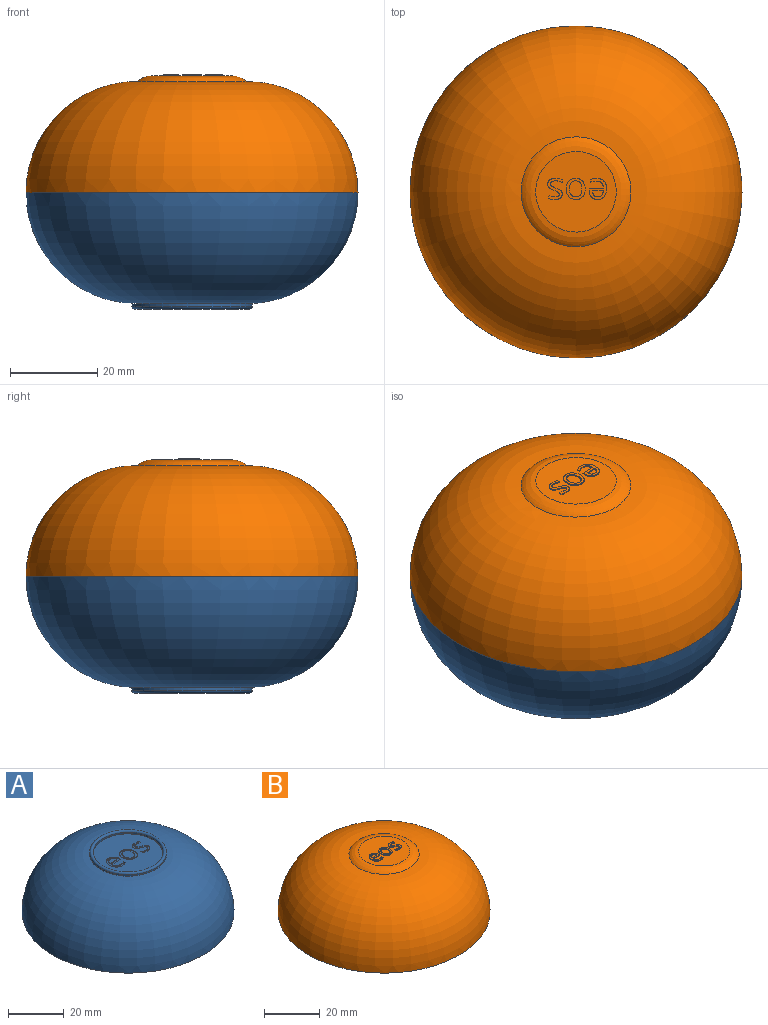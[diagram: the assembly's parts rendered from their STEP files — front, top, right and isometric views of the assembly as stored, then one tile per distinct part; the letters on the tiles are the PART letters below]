
ASSEMBLY  parts=2 mates=1
PART A: 74 faces, bbox 75.9x75.9x26.7 mm
  f0: plane 24.98x24.98mm, normal (0,0,1), area 425.6mm2, adj f4,f14,f15,f16,f17,f18,f19,f20
  f1: plane 75.95x75.95mm, normal (0,0,-1), area 339mm2, adj f2,f73
  f2: torus R=12.57mm, axis (0,0,1), area 7205.7mm2, adj f1,f5
  f3: cylinder r=13.76mm len=27.52mm, axis (0,0,-1), area 54.9mm2, adj f5,f6
  f4: cylinder r=12.49mm len=24.98mm, axis (0,0,-1), area 49.8mm2, adj f0,f6
  f5: plane 27.52x27.52mm, normal (0,0,-1), area 98mm2, adj f2,f3
  f6: torus R=13.12mm, axis (0,0,1), area 164.5mm2, adj f3,f4
  f7: extruded ~1.85x0.49mm, area 0.5mm2, adj f8,f23,f24,f71
  f8: extruded ~1.84x0.48mm, area 0.5mm2, adj f7,f9,f24,f71
  f9: extruded ~1.42x0.62mm, area 0.4mm2, adj f8,f10,f24,f71
  f10: extruded ~1.44x0.63mm, area 0.4mm2, adj f9,f11,f24,f71
  f11: extruded ~1.83x0.49mm, area 0.5mm2, adj f10,f12,f24,f71
  f12: extruded ~1.85x0.49mm, area 0.5mm2, adj f11,f13,f24,f71
  f13: extruded ~1.43x0.63mm, area 0.4mm2, adj f12,f23,f24,f71
  f14: extruded ~2.42x0.78mm, area 0.7mm2, adj f0,f15,f22,f24
  f15: extruded ~2.39x0.78mm, area 0.7mm2, adj f0,f14,f16,f24
  f16: extruded ~2.11x0.88mm, area 0.6mm2, adj f0,f15,f17,f24
  f17: extruded ~2.15x0.86mm, area 0.6mm2, adj f0,f16,f18,f24
  f18: extruded ~2.41x0.77mm, area 0.7mm2, adj f0,f17,f19,f24
  f19: extruded ~1.74x0.36mm, area 0.5mm2, adj f0,f18,f20,f24
  f20: extruded ~1.14x1.02mm, area 0.4mm2, adj f0,f19,f21,f24
  f21: extruded ~1.51x0.4mm, area 0.4mm2, adj f0,f20,f22,f24
  f22: extruded ~2.15x0.87mm, area 0.6mm2, adj f0,f14,f21,f24
  f23: extruded ~1.43x0.63mm, area 0.4mm2, adj f7,f13,f24,f71
  f24: plane 6.56x5.81mm, normal (0,0,1), area 15.4mm2, adj f7,f8,f9,f10,f11,f12,f13,f14
  f25: extruded ~1.21x0.5mm, area 0.3mm2, adj f26,f43,f44,f72
  f26: extruded ~1.16x0.48mm, area 0.3mm2, adj f25,f27,f44,f72
  f27: extruded ~1.39x0.4mm, area 0.4mm2, adj f26,f28,f44,f72
  f28: plane 3.31x0.25mm, normal (0,-1,0), area 0.8mm2, adj f27,f43,f44,f72
  f29: extruded ~2.21x0.86mm, area 0.6mm2, adj f0,f30,f42,f44
  f30: extruded ~1.09x0.25mm, area 0.3mm2, adj f0,f29,f31,f44
  f31: extruded ~0.96x0.31mm, area 0.3mm2, adj f0,f30,f32,f44
  f32: plane 0.86x0.25mm, normal (-1,0,0), area 0.2mm2, adj f0,f31,f33,f44
  f33: extruded ~2.02x0.43mm, area 0.5mm2, adj f0,f32,f34,f44
  f34: extruded ~1.5x0.58mm, area 0.4mm2, adj f0,f33,f35,f44
  f35: extruded ~1.69x0.56mm, area 0.5mm2, adj f0,f34,f36,f44
  f36: plane 4.36x0.25mm, normal (0,1,0), area 1.1mm2, adj f0,f35,f37,f44
  f37: plane 0.61x0.25mm, normal (-1,0,0), area 0.2mm2, adj f0,f36,f38,f44
  f38: extruded ~2.06x0.69mm, area 0.6mm2, adj f0,f37,f39,f44
  f39: extruded ~1.88x0.78mm, area 0.5mm2, adj f0,f38,f40,f44
  f40: extruded ~2.03x0.9mm, area 0.6mm2, adj f0,f39,f41,f44
  f41: extruded ~2.43x0.75mm, area 0.7mm2, adj f0,f40,f42,f44
  f42: extruded ~2.37x0.81mm, area 0.7mm2, adj f0,f29,f41,f44
  f43: extruded ~1.37x0.54mm, area 0.4mm2, adj f25,f28,f44,f72
  f44: plane 6.56x5.35mm, normal (0,0,1), area 16mm2, adj f25,f26,f27,f28,f29,f30,f31,f32
  f45: extruded ~1.36x0.66mm, area 0.4mm2, adj f0,f46,f69,f70
  f46: extruded ~1.05x0.4mm, area 0.3mm2, adj f0,f45,f47,f70
  f47: extruded ~1.52x0.83mm, area 0.4mm2, adj f0,f46,f48,f70
  f48: extruded ~1.11x0.47mm, area 0.3mm2, adj f0,f47,f49,f70
  f49: extruded ~0.42x0.34mm, area 0.1mm2, adj f0,f48,f50,f70
  f50: extruded ~0.43x0.25mm, area 0.1mm2, adj f0,f49,f51,f70
  f51: extruded ~0.59x0.35mm, area 0.2mm2, adj f0,f50,f52,f70
  f52: extruded ~1.03x0.25mm, area 0.3mm2, adj f0,f51,f53,f70
  f53: extruded ~1.73x0.39mm, area 0.5mm2, adj f0,f52,f54,f70
  f54: plane 0.78x0.34mm, normal (-0.92,0.4,0), area 0.2mm2, adj f0,f53,f55,f70
  f55: extruded ~2x0.42mm, area 0.5mm2, adj f0,f54,f56,f70
  f56: extruded ~1.73x0.45mm, area 0.5mm2, adj f0,f55,f57,f70
  f57: extruded ~1.22x0.63mm, area 0.4mm2, adj f0,f56,f58,f70
  f58: extruded ~0.74x0.25mm, area 0.2mm2, adj f0,f57,f59,f70
  f59: extruded ~0.56x0.55mm, area 0.2mm2, adj f0,f58,f60,f70
  f60: extruded ~1.26x0.57mm, area 0.4mm2, adj f0,f59,f61,f70
  f61: extruded ~1.25x0.62mm, area 0.4mm2, adj f0,f60,f62,f70
  f62: extruded ~0.63x0.32mm, area 0.2mm2, adj f0,f61,f63,f70
  f63: extruded ~0.73x0.4mm, area 0.2mm2, adj f0,f62,f64,f70
  f64: extruded ~1.15x0.25mm, area 0.3mm2, adj f0,f63,f65,f70
  f65: extruded ~1.01x0.25mm, area 0.3mm2, adj f0,f64,f66,f70
  f66: extruded ~0.98x0.36mm, area 0.3mm2, adj f0,f65,f67,f70
  f67: plane 0.89x0.25mm, normal (1,0,0), area 0.2mm2, adj f0,f66,f68,f70
  f68: extruded ~1.96x0.4mm, area 0.5mm2, adj f0,f67,f69,f70
  f69: extruded ~1.85x0.48mm, area 0.5mm2, adj f0,f45,f68,f70
  f70: plane 6.56x4.49mm, normal (0,0,1), area 12.3mm2, adj f45,f46,f47,f48,f49,f50,f51,f52
  f71: plane 4.94x3.83mm, normal (0,0,1), area 15.7mm2, adj f7,f8,f9,f10,f11,f12,f13,f23
  f72: plane 3.31x1.87mm, normal (0,0,1), area 5mm2, adj f25,f26,f27,f28,f43
  f73: sphere r=40.23mm, area 5905.9mm2, adj f1
PART B: 71 faces, bbox 75.9x75.9x26.9 mm
  f0: plane 18.43x18.43mm, normal (0,0,1), area 231.5mm2, adj f3,f8,f9,f10,f11,f12,f13,f14
  f1: plane 75.95x75.95mm, normal (0,0,-1), area 338.8mm2, adj f2,f70
  f2: torus R=12.57mm, axis (0,0,1), area 7205.6mm2, adj f1,f3
  f3: torus R=9.21mm, axis (0,0,-1), area 253.1mm2, adj f0,f2
  f4: extruded ~0.9x0.37mm, area 0.3mm2, adj f5,f22,f23,f24
  f5: extruded ~0.85x0.36mm, area 0.2mm2, adj f4,f6,f23,f24
  f6: extruded ~1.03x0.3mm, area 0.3mm2, adj f5,f7,f23,f24
  f7: plane 2.45x0.25mm, normal (0,1,0), area 0.6mm2, adj f6,f22,f23,f24
  f8: extruded ~1.64x0.63mm, area 0.5mm2, adj f0,f9,f21,f23
  f9: extruded ~0.81x0.25mm, area 0.2mm2, adj f0,f8,f10,f23
  f10: extruded ~0.71x0.25mm, area 0.2mm2, adj f0,f9,f11,f23
  f11: plane 0.63x0.25mm, normal (1,0,0), area 0.2mm2, adj f0,f10,f12,f23
  f12: extruded ~1.49x0.32mm, area 0.4mm2, adj f0,f11,f13,f23
  f13: extruded ~1.11x0.43mm, area 0.3mm2, adj f0,f12,f14,f23
  f14: extruded ~1.25x0.42mm, area 0.3mm2, adj f0,f13,f15,f23
  f15: plane 3.22x0.25mm, normal (0,-1,0), area 0.8mm2, adj f0,f14,f16,f23
  f16: plane 0.45x0.25mm, normal (1,0,0), area 0.1mm2, adj f0,f15,f17,f23
  f17: extruded ~1.53x0.51mm, area 0.4mm2, adj f0,f16,f18,f23
  f18: extruded ~1.39x0.58mm, area 0.4mm2, adj f0,f17,f19,f23
  f19: extruded ~1.5x0.67mm, area 0.4mm2, adj f0,f18,f20,f23
  f20: extruded ~1.8x0.56mm, area 0.5mm2, adj f0,f19,f21,f23
  f21: extruded ~1.75x0.6mm, area 0.5mm2, adj f0,f8,f20,f23
  f22: extruded ~1.02x0.4mm, area 0.3mm2, adj f4,f7,f23,f24
  f23: plane 4.85x3.96mm, normal (0,0,1), area 8.7mm2, adj f4,f5,f6,f7,f8,f9,f10,f11
  f24: plane 2.45x1.38mm, normal (0,0,1), area 2.7mm2, adj f4,f5,f6,f7,f22
  f25: extruded ~1.37x0.36mm, area 0.4mm2, adj f26,f41,f42,f43
  f26: extruded ~1.36x0.35mm, area 0.4mm2, adj f25,f27,f42,f43
  f27: extruded ~1.05x0.46mm, area 0.3mm2, adj f26,f28,f42,f43
  f28: extruded ~1.07x0.46mm, area 0.3mm2, adj f27,f29,f42,f43
  f29: extruded ~1.36x0.36mm, area 0.4mm2, adj f28,f30,f42,f43
  f30: extruded ~1.37x0.36mm, area 0.4mm2, adj f29,f31,f42,f43
  f31: extruded ~1.06x0.47mm, area 0.3mm2, adj f30,f41,f42,f43
  f32: extruded ~1.79x0.58mm, area 0.5mm2, adj f0,f33,f40,f42
  f33: extruded ~1.77x0.58mm, area 0.5mm2, adj f0,f32,f34,f42
  f34: extruded ~1.56x0.65mm, area 0.4mm2, adj f0,f33,f35,f42
  f35: extruded ~1.59x0.64mm, area 0.4mm2, adj f0,f34,f36,f42
  f36: extruded ~1.78x0.57mm, area 0.5mm2, adj f0,f35,f37,f42
  f37: extruded ~1.29x0.27mm, area 0.3mm2, adj f0,f36,f38,f42
  f38: extruded ~0.85x0.75mm, area 0.3mm2, adj f0,f37,f39,f42
  f39: extruded ~1.12x0.3mm, area 0.3mm2, adj f0,f38,f40,f42
  f40: extruded ~1.59x0.64mm, area 0.5mm2, adj f0,f32,f39,f42
  f41: extruded ~1.05x0.47mm, area 0.3mm2, adj f25,f31,f42,f43
  f42: plane 4.85x4.3mm, normal (0,0,1), area 8.4mm2, adj f25,f26,f27,f28,f29,f30,f31,f32
  f43: plane 3.65x2.83mm, normal (0,0,1), area 8.6mm2, adj f25,f26,f27,f28,f29,f30,f31,f41
  f44: extruded ~1.01x0.49mm, area 0.3mm2, adj f0,f45,f68,f69
  f45: extruded ~0.77x0.29mm, area 0.2mm2, adj f0,f44,f46,f69
  f46: extruded ~1.12x0.61mm, area 0.3mm2, adj f0,f45,f47,f69
  f47: extruded ~0.82x0.35mm, area 0.2mm2, adj f0,f46,f48,f69
  f48: extruded ~0.31x0.25mm, area 0.1mm2, adj f0,f47,f49,f69
  f49: extruded ~0.32x0.25mm, area 0.1mm2, adj f0,f48,f50,f69
  f50: extruded ~0.44x0.26mm, area 0.1mm2, adj f0,f49,f51,f69
  f51: extruded ~0.76x0.25mm, area 0.2mm2, adj f0,f50,f52,f69
  f52: extruded ~1.28x0.29mm, area 0.3mm2, adj f0,f51,f53,f69
  f53: plane 0.58x0.25mm, normal (0.92,-0.4,0), area 0.2mm2, adj f0,f52,f54,f69
  f54: extruded ~1.48x0.31mm, area 0.4mm2, adj f0,f53,f55,f69
  f55: extruded ~1.28x0.33mm, area 0.3mm2, adj f0,f54,f56,f69
  f56: extruded ~0.9x0.47mm, area 0.3mm2, adj f0,f55,f57,f69
  f57: extruded ~0.55x0.25mm, area 0.1mm2, adj f0,f56,f58,f69
  f58: extruded ~0.41x0.41mm, area 0.1mm2, adj f0,f57,f59,f69
  f59: extruded ~0.93x0.43mm, area 0.3mm2, adj f0,f58,f60,f69
  f60: extruded ~0.93x0.46mm, area 0.3mm2, adj f0,f59,f61,f69
  f61: extruded ~0.47x0.25mm, area 0.1mm2, adj f0,f60,f62,f69
  f62: extruded ~0.54x0.3mm, area 0.2mm2, adj f0,f61,f63,f69
  f63: extruded ~0.85x0.25mm, area 0.2mm2, adj f0,f62,f64,f69
  f64: extruded ~0.75x0.25mm, area 0.2mm2, adj f0,f63,f65,f69
  f65: extruded ~0.72x0.27mm, area 0.2mm2, adj f0,f64,f66,f69
  f66: plane 0.66x0.25mm, normal (-1,0,0), area 0.2mm2, adj f0,f65,f67,f69
  f67: extruded ~1.45x0.3mm, area 0.4mm2, adj f0,f66,f68,f69
  f68: extruded ~1.37x0.35mm, area 0.4mm2, adj f0,f44,f67,f69
  f69: plane 4.85x3.32mm, normal (0,0,1), area 6.7mm2, adj f44,f45,f46,f47,f48,f49,f50,f51
  f70: sphere r=40.25mm, area 5902.9mm2, adj f1
PLACE A rot(axis=(1,0,0),180deg) t=(-97.62,-70.2,49.69)mm
PLACE B rot(axis=(0,0,1),180deg) t=(-97.62,-70.2,49.69)mm
MATE cylindrical A.f2 <-> B.f2  axis (0,0,1) through (-97.62,-70.2,49.69)mm
